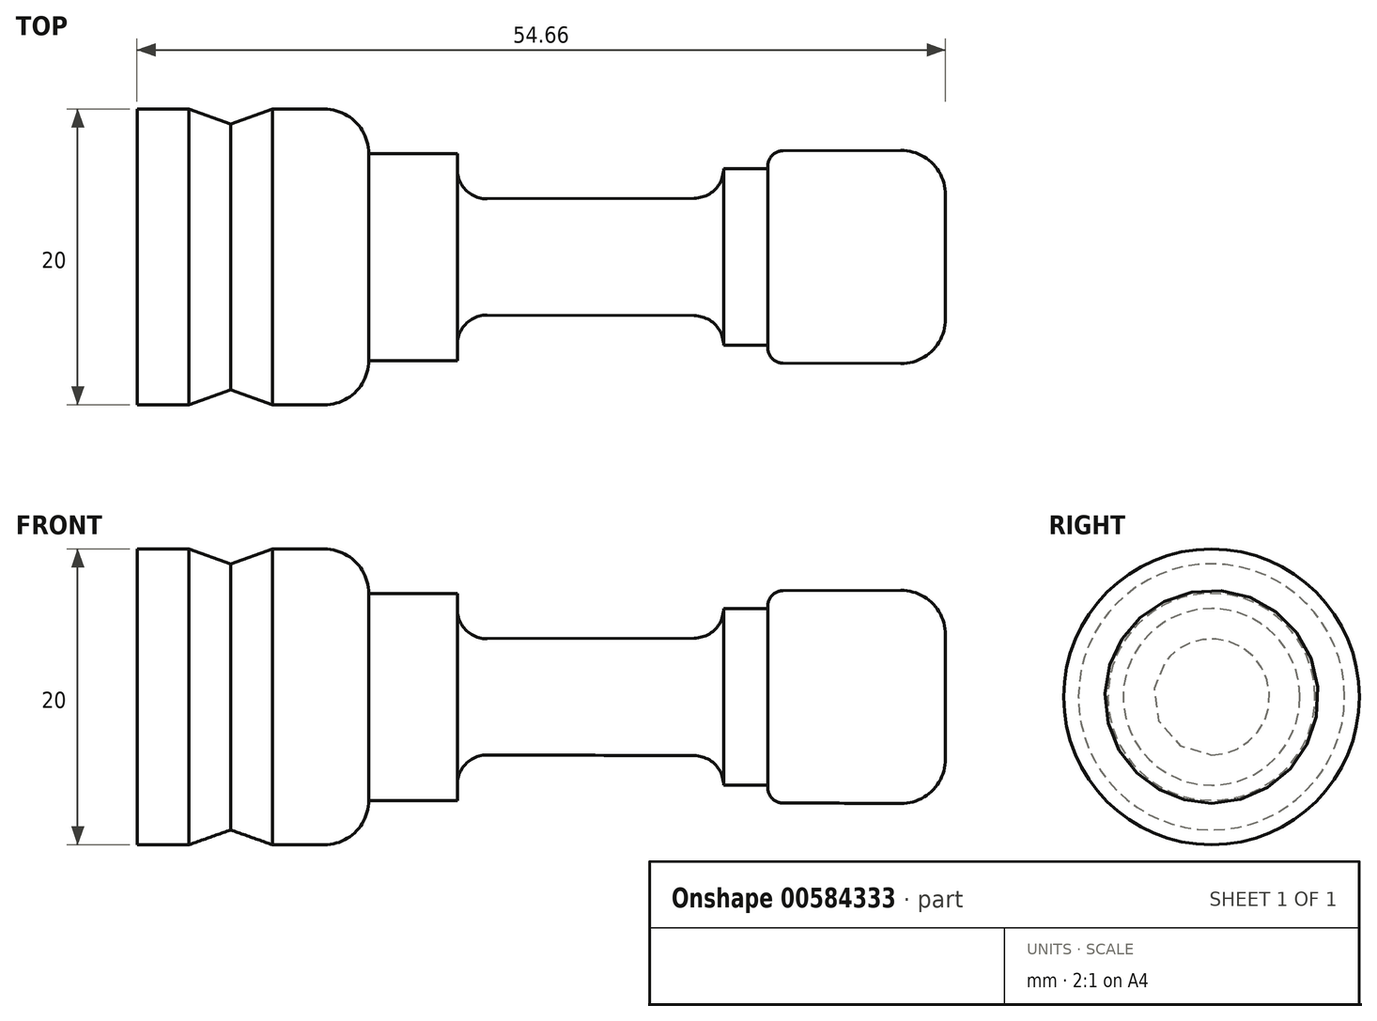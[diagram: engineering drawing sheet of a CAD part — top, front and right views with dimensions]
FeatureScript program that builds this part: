
annotation { "Feature Type Name" : "Feature", "Feature Type Description" : "" }
export const myFeature = defineFeature(function(context is Context, id is Id, definition is map)
    precondition{}
    {
        {
            var Q0;
            Q0=qCreatedBy(makeId("Front.planeOp"),FACE);
            var sketch = newSketch(context, id + "F0", { "sketchPlane" : qUnion([Q0])});
            skLineSegment(sketch, "E0", {"start": v(-60.72, 10) * mm, "end": v(-60.72, 0) * mm});
            skLineSegment(sketch, "E1", {"start": v(-57.22, 0) * mm, "end": v(-60.72, 0) * mm});
            skLineSegment(sketch, "E2", {"start": v(-57.22, 0) * mm, "end": v(-54.38, 1) * mm});
            skLineSegment(sketch, "E3", {"start": v(-54.38, 1) * mm, "end": v(-51.56, 0) * mm});
            skLineSegment(sketch, "E4", {"start": v(-48.06, 0) * mm, "end": v(-51.56, 0) * mm});
            skPoint(sketch, "E5.visualSharp", {"position": v(-45.06, 0) * mm});
            skArc(sketch, "E5.filletArc", {"start": v(-48.06, 0) * mm, "mid": v(-45.93, 0.88) * mm, "end": v(-45.06, 3) * mm});
            skLineSegment(sketch, "E6", {"start": v(-45.06, 3) * mm, "end": v(-39.06, 3) * mm});
            skPoint(sketch, "E7.start.orphan", {"position": v(-39.06, 1.4) * mm});
            skLineSegment(sketch, "E8", {"start": v(-23.05, 6.03) * mm, "end": v(-37.05, 6.08) * mm});
            skArc(sketch, "E9.filletArc", {"start": v(-37.05, 6.08) * mm, "mid": v(-38.47, 5.5) * mm, "end": v(-39.06, 4.08) * mm});
            skArc(sketch, "E10.filletArc", {"start": v(-21.06, 4.03) * mm, "mid": v(-21.64, 5.44) * mm, "end": v(-23.05, 6.03) * mm});
            skLineSegment(sketch, "E11", {"start": v(-18.06, 4.03) * mm, "end": v(-21.06, 4.03) * mm});
            skLineSegment(sketch, "E12", {"start": v(-17.06, 2.82) * mm, "end": v(-9.07, 2.8) * mm});
            skPoint(sketch, "E13.visualSharp", {"position": v(-18.06, 2.83) * mm});
            skArc(sketch, "E13.filletArc", {"start": v(-18.06, 3.82) * mm, "mid": v(-17.76, 3.12) * mm, "end": v(-17.06, 2.82) * mm});
            skPoint(sketch, "E14.visualSharp", {"position": v(-6.06, 2.78) * mm});
            skArc(sketch, "E14.filletArc", {"start": v(-9.07, 2.8) * mm, "mid": v(-6.94, 3.67) * mm, "end": v(-6.06, 5.8) * mm});
            skLineSegment(sketch, "E15", {"start": v(-60.72, 10) * mm, "end": v(-6.06, 10) * mm});
            skLineSegment(sketch, "E16", {"start": v(-6.06, 10) * mm, "end": v(-6.06, 5.8) * mm});
            skLineSegment(sketch, "E17", {"start": v(-60.72, 10) * mm, "end": v(-63.83, 10) * mm, "construction": true});
            skLineSegment(sketch, "E18", {"start": v(-18.06, 4.03) * mm, "end": v(-18.06, 3.82) * mm});
            skLineSegment(sketch, "E19", {"start": v(-39.06, 4.08) * mm, "end": v(-39.06, 3) * mm});
            skSolve(sketch);
        }
        {
            var Q0;
            Q0=makeQuery(id+"F0.imprint","IMPRINT",FACE,{"disambiguationData":[TD([[makeQuery(id+"F0.imprint","IMPRINT",EDGE,{"derivedFrom":sQuery(id+"F0.wireOp",EDGE,"E0")}),1.0]])]});
            var Q1;
            Q1=sQuery(id+"F0.wireOp",EDGE,"E17");
            revolve(context, id + "F1", {"entities" : qUnion([Q0]), "axis" : qUnion([Q1]), "revolveType" : RevolveType.FULL});
        }
    });
